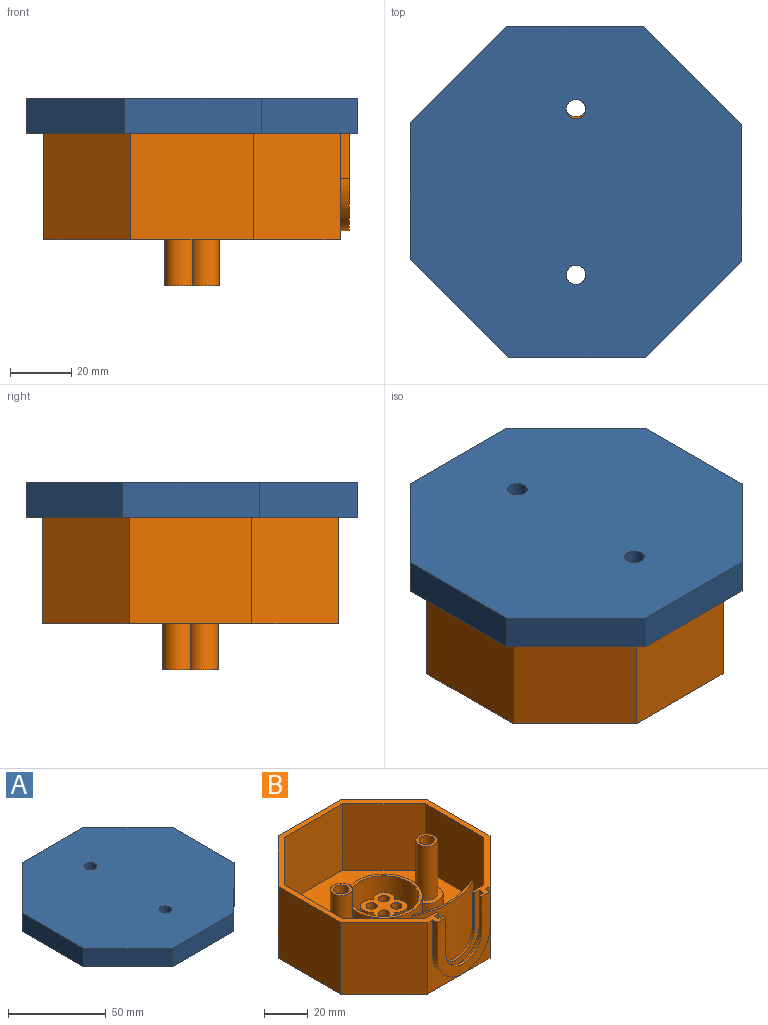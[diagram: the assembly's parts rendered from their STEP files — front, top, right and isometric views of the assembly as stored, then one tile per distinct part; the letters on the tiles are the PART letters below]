
ASSEMBLY  parts=2 mates=1
PART A: 45 faces, bbox 108x108x21 mm
  f0: plane 31.43x31.43mm, normal (-0.71,0.71,0), area 508.1mm2, adj f1,f7,f8,f9
  f1: plane 44.45x11.43mm, normal (-1,0,0), area 508.1mm2, adj f0,f2,f8,f9
  f2: plane 32.07x32.07mm, normal (-0.71,-0.71,0), area 518.4mm2, adj f1,f3,f8,f9
  f3: plane 44.45x11.43mm, normal (0,-1,0), area 508.1mm2, adj f2,f4,f8,f9
  f4: plane 31.43x31.43mm, normal (0.71,-0.71,0), area 508.1mm2, adj f3,f5,f8,f9
  f5: plane 44.45x11.43mm, normal (1,0,0), area 508.1mm2, adj f4,f6,f8,f9
  f6: plane 32.07x32.07mm, normal (0.71,0.71,0), area 518.4mm2, adj f5,f7,f8,f9
  f7: plane 44.45x11.43mm, normal (0,1,0), area 508.1mm2, adj f0,f6,f8,f9
  f8: plane 107.95x107.95mm, normal (0,0,1), area 9573.5mm2, adj f0,f1,f2,f3,f4,f5,f6,f7
  f9: plane 107.95x107.95mm, normal (0,0,-1), area 1120.4mm2, adj f0,f1,f2,f3,f4,f5,f6,f7
  f10: plane 29.57x29.57mm, normal (0.71,-0.71,0), area 132.8mm2, adj f9,f11,f17,f18
  f11: plane 41.82x3.18mm, normal (0,-1,0), area 132.8mm2, adj f9,f10,f12,f18
  f12: plane 30.21x30.21mm, normal (-0.71,-0.71,0), area 135.6mm2, adj f9,f11,f13,f18
  f13: plane 41.18x3.18mm, normal (-1,0,0), area 130.8mm2, adj f9,f12,f14,f18
  f14: plane 30.21x30.21mm, normal (-0.71,0.71,0), area 135.6mm2, adj f9,f13,f15,f18
  f15: plane 41.18x3.18mm, normal (0,1,0), area 130.8mm2, adj f9,f14,f16,f18
  f16: plane 30.21x30.21mm, normal (0.71,0.71,0), area 135.6mm2, adj f9,f15,f17,f18
  f17: plane 41.82x3.18mm, normal (1,0,0), area 132.8mm2, adj f9,f10,f16,f18
  f18: plane 101.6x101.6mm, normal (0,0,-1), area 7495.1mm2, adj f10,f11,f12,f13,f14,f15,f16,f17
  f19: cylinder r=3.17mm len=8.26mm, axis (0,0,-1), area 164.7mm2, adj f8,f18
  f20: cylinder r=3.17mm len=8.26mm, axis (0,0,-1), area 164.7mm2, adj f8,f18
  f21: cylinder r=17.46mm len=34.93mm, axis (0,0,1), area 1393.4mm2, adj f18,f22
  f22: plane 34.93x34.93mm, normal (0,0,-1), area 134.3mm2, adj f21,f44
  f23: plane 30.69x30.69mm, normal (0.71,-0.71,0), area 385.8mm2, adj f24,f30,f31,f32
  f24: plane 43.4x8.89mm, normal (1,0,0), area 385.8mm2, adj f23,f25,f31,f32
  f25: plane 31.33x31.33mm, normal (0.71,0.71,0), area 393.8mm2, adj f24,f26,f31,f32
  f26: plane 43.4x8.89mm, normal (0,1,0), area 385.8mm2, adj f25,f27,f31,f32
  f27: plane 30.69x30.69mm, normal (-0.71,0.71,0), area 385.8mm2, adj f26,f28,f31,f32
  f28: plane 43.4x8.89mm, normal (-1,0,0), area 385.8mm2, adj f27,f29,f31,f32
  f29: plane 31.33x31.33mm, normal (-0.71,-0.71,0), area 393.8mm2, adj f28,f30,f31,f32
  f30: plane 43.4x8.89mm, normal (0,-1,0), area 385.8mm2, adj f23,f29,f31,f32
  f31: plane 105.41x105.41mm, normal (0,0,-1), area 9064.2mm2, adj f23,f24,f25,f26,f27,f28,f29,f30
  f32: plane 105.41x105.41mm, normal (0,0,1), area 239.8mm2, adj f23,f24,f25,f26,f27,f28,f29,f30
  f33: plane 30.32x30.32mm, normal (-0.71,0.71,0), area 136.1mm2, adj f32,f34,f40,f41
  f34: plane 42.87x3.18mm, normal (0,1,0), area 136.1mm2, adj f32,f33,f35,f41
  f35: plane 30.95x30.95mm, normal (0.71,0.71,0), area 139mm2, adj f32,f34,f36,f41
  f36: plane 42.23x3.18mm, normal (1,0,0), area 134.1mm2, adj f32,f35,f37,f41
  f37: plane 30.95x30.95mm, normal (0.71,-0.71,0), area 139mm2, adj f32,f36,f38,f41
  f38: plane 42.23x3.18mm, normal (0,-1,0), area 134.1mm2, adj f32,f37,f39,f41
  f39: plane 30.95x30.95mm, normal (-0.71,-0.71,0), area 139mm2, adj f32,f38,f40,f41
  f40: plane 42.87x3.18mm, normal (-1,0,0), area 136.1mm2, adj f32,f33,f39,f41
  f41: plane 104.14x104.14mm, normal (0,0,1), area 8000.6mm2, adj f33,f34,f35,f36,f37,f38,f39,f40
  f42: cylinder r=4.45mm len=8.89mm, axis (0,0,-1), area 159.6mm2, adj f31,f41
  f43: cylinder r=4.45mm len=8.89mm, axis (0,0,-1), area 159.6mm2, adj f31,f41
  f44: cylinder r=16.19mm len=32.39mm, axis (0,0,1), area 1421.3mm2, adj f22,f41
PART B: 68 faces, bbox 96.6x99.6x55 mm
  f0: plane 37.51x37mm, normal (0,1,0), area 720.3mm2, adj f1,f3,f15,f16,f65,f66,f67
  f1: plane 99.57x96.57mm, normal (0,0,1), area 876.2mm2, adj f0,f2,f4,f5,f6,f7,f8,f9
  f2: plane 40x40mm, normal (0,-1,0), area 466mm2, adj f1,f7,f8,f11,f52,f53,f54
  f3: plane 90.57x90.57mm, normal (0,0,1), area 5444.7mm2, adj f0,f12,f13,f14,f15,f16,f17,f18
  f4: plane 40x40mm, normal (0,1,0), area 1600mm2, adj f1,f5,f10,f11
  f5: plane 40x28.28mm, normal (-0.71,0.71,0), area 1600mm2, adj f1,f4,f6,f11
  f6: plane 40x40mm, normal (-1,0,0), area 1600mm2, adj f1,f5,f7,f11
  f7: plane 40x28.28mm, normal (-0.71,-0.71,0), area 1600mm2, adj f1,f2,f6,f11
  f8: plane 40x28.28mm, normal (0.71,-0.71,0), area 1600mm2, adj f1,f2,f9,f11
  f9: plane 40x40mm, normal (1,0,0), area 1600mm2, adj f1,f8,f10,f11
  f10: plane 40x28.28mm, normal (0.71,0.71,0), area 1600mm2, adj f1,f4,f9,f11
  f11: plane 96.57x96.57mm, normal (0,0,-1), area 7365.2mm2, adj f2,f4,f5,f6,f7,f8,f9,f10
  f12: plane 37.51x37mm, normal (0,-1,0), area 1388mm2, adj f1,f3,f13,f18
  f13: plane 37x26.53mm, normal (0.71,-0.71,0), area 1388mm2, adj f1,f3,f12,f14
  f14: plane 37.51x37mm, normal (1,0,0), area 1388mm2, adj f1,f3,f13,f15
  f15: plane 37x26.53mm, normal (0.71,0.71,0), area 1388mm2, adj f0,f1,f3,f14
  f16: plane 37x26.53mm, normal (-0.71,0.71,0), area 1388mm2, adj f0,f1,f3,f17
  f17: plane 37.51x37mm, normal (-1,0,0), area 1388mm2, adj f1,f3,f16,f18
  f18: plane 37x26.53mm, normal (-0.71,-0.71,0), area 1388mm2, adj f1,f3,f12,f17
  f19: cylinder r=17.46mm len=34.93mm, axis (0,0,-1), area 1920.1mm2, adj f3,f20
  f20: plane 34.93x34.93mm, normal (0,0,1), area 157.5mm2, adj f19,f22
  f21: plane 31.93x31.93mm, normal (0,0,1), area 517.2mm2, adj f22,f24,f25,f26,f27
  f22: cylinder r=15.96mm len=31.93mm, axis (0,0,-1), area 1905.6mm2, adj f20,f21
  f23: plane 18x18mm, normal (0,0,1), area 204.7mm2, adj f24,f25,f26,f27,f31,f32,f33,f34
  f24: cylinder r=5mm len=13.5mm, axis (0,0,1), area 231.2mm2, adj f21,f23,f25,f27
  f25: cylinder r=5mm len=13.5mm, axis (0,0,1), area 231.2mm2, adj f21,f23,f24,f26
  f26: cylinder r=5mm len=13.5mm, axis (0,0,1), area 231.2mm2, adj f21,f23,f25,f27
  f27: cylinder r=5mm len=13.5mm, axis (0,0,1), area 231.2mm2, adj f21,f23,f24,f26
  f28: cylinder r=5mm len=15mm, axis (0,0,1), area 256.9mm2, adj f11,f29,f35,f36
  f29: cylinder r=5mm len=15mm, axis (0,0,1), area 256.9mm2, adj f11,f28,f30,f36
  f30: cylinder r=5mm len=15mm, axis (0,0,1), area 256.9mm2, adj f11,f29,f35,f36
  f31: cylinder r=2.5mm len=30mm, axis (0,0,1), area 471.2mm2, adj f23,f36
  f32: cylinder r=2.5mm len=30mm, axis (0,0,1), area 471.2mm2, adj f23,f36
  f33: cylinder r=2.5mm len=30mm, axis (0,0,1), area 471.2mm2, adj f23,f36
  f34: cylinder r=2.5mm len=30mm, axis (0,0,1), area 471.2mm2, adj f23,f36
  f35: cylinder r=5mm len=15mm, axis (0,0,1), area 256.9mm2, adj f11,f28,f30,f36
  f36: plane 18x18mm, normal (0,0,-1), area 204.7mm2, adj f28,f29,f30,f31,f32,f33,f34,f35
  f37: cylinder r=7.5mm len=15mm, axis (0,0,-1), area 235.6mm2, adj f3,f38
  f38: plane 15x15mm, normal (0,0,1), area 98.2mm2, adj f37,f40
  f39: plane 10x10mm, normal (0,0,1), area 40.1mm2, adj f40,f46
  f40: cylinder r=5mm len=30mm, axis (0,0,-1), area 942.5mm2, adj f38,f39
  f41: cylinder r=7.5mm len=15mm, axis (0,0,-1), area 235.6mm2, adj f3,f42
  f42: plane 15x15mm, normal (0,0,1), area 98.2mm2, adj f41,f44
  f43: plane 10x10mm, normal (0,0,1), area 40.1mm2, adj f44,f45
  f44: cylinder r=5mm len=30mm, axis (0,0,-1), area 942.5mm2, adj f42,f43
  f45: cylinder r=3.5mm len=38mm, axis (0,0,1), area 835.7mm2, adj f11,f43
  f46: cylinder r=3.5mm len=38mm, axis (0,0,1), area 835.7mm2, adj f11,f39
  f47: plane 35x2.22mm, normal (0,1,0), area 77.8mm2, adj f3,f48,f50,f51
  f48: cylinder r=42.5mm len=40mm, axis (0,0,-1), area 1457.6mm2, adj f3,f47,f49,f51
  f49: plane 35x2.22mm, normal (0,1,0), area 77.8mm2, adj f3,f48,f50,f51
  f50: cylinder r=41.5mm len=35.55mm, axis (0,0,-1), area 1285.9mm2, adj f3,f47,f49,f51
  f51: plane 40x5mm, normal (0,0,1), area 39.2mm2, adj f47,f48,f49,f50
  f52: plane 20x3mm, normal (-1,0,0), area 60mm2, adj f1,f2,f53,f55
  f53: cylinder r=17mm len=34mm, axis (0,1,0), area 160.2mm2, adj f2,f52,f54,f55
  f54: plane 20x3mm, normal (1,0,0), area 60mm2, adj f1,f2,f53,f55
  f55: plane 37x34mm, normal (0,-1,0), area 466.2mm2, adj f1,f52,f53,f54,f62,f63,f64
  f56: plane 18.62x3mm, normal (1,0,0), area 55.9mm2, adj f1,f57,f60,f61
  f57: cylinder r=14.5mm len=29mm, axis (0,-1,0), area 140.8mm2, adj f56,f58,f60,f61
  f58: plane 3x0.07mm, normal (0,0,1), area 0.2mm2, adj f57,f59,f60,f61
  f59: plane 20x3mm, normal (-1,0,0), area 60mm2, adj f1,f58,f60,f61
  f60: plane 34.5x29.07mm, normal (0,-1,0), area 242.6mm2, adj f1,f56,f57,f58,f59,f65,f66,f67
  f61: plane 34.5x29.07mm, normal (0,1,0), area 242.6mm2, adj f1,f56,f57,f58,f59,f62,f63,f64
  f62: plane 20x1.5mm, normal (-1,0,0), area 30mm2, adj f1,f55,f61,f63
  f63: cylinder r=11.5mm len=23mm, axis (0,-1,0), area 54.2mm2, adj f55,f61,f62,f64
  f64: plane 20x1.5mm, normal (1,0,0), area 30mm2, adj f1,f55,f61,f63
  f65: plane 20x1.5mm, normal (1,0,0), area 30mm2, adj f0,f1,f60,f67
  f66: plane 20x1.5mm, normal (-1,0,0), area 30mm2, adj f0,f1,f60,f67
  f67: cylinder r=11.5mm len=23mm, axis (0,-1,0), area 54.2mm2, adj f0,f60,f65,f66
PLACE A t=(-14.29,-16.69,-31.36)mm
PLACE B rot(axis=(0,0,1),90deg) t=(-14.29,-16.18,-66.18)mm
MATE revolute B.f46 <-> A.f19  axis (0,0,1) through (-14.29,-43.68,-28.18)mm
